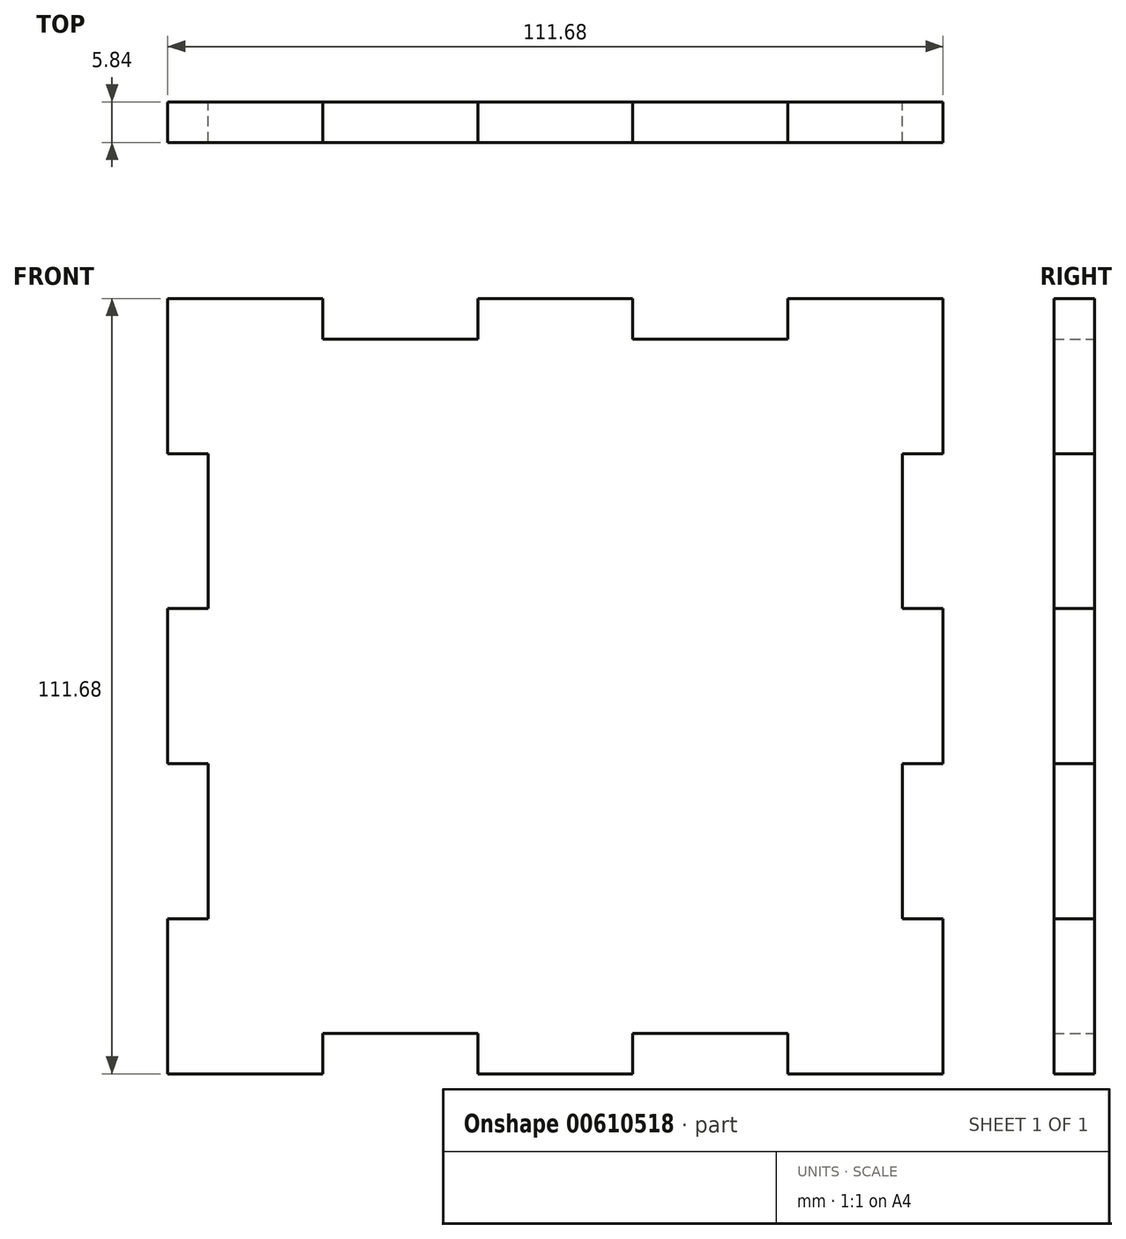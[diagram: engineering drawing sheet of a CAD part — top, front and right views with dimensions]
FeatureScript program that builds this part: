
annotation { "Feature Type Name" : "Feature", "Feature Type Description" : "" }
export const myFeature = defineFeature(function(context is Context, id is Id, definition is map)
    precondition{}
    {
        {
            var Q0;
            Q0=qCreatedBy(makeId("Front.planeOp"),FACE);
            var sketch = newSketch(context, id + "F0", { "sketchPlane" : qUnion([Q0])});
            skLineSegment(sketch, "E0.bottom", {"start": v(-50, 50) * mm, "end": v(50, 50) * mm});
            skLineSegment(sketch, "E0.top", {"start": v(-50, -50) * mm, "end": v(50, -50) * mm});
            skLineSegment(sketch, "E0.left", {"start": v(-50, 50) * mm, "end": v(-50, -50) * mm});
            skLineSegment(sketch, "E0.right", {"start": v(50, 50) * mm, "end": v(50, -50) * mm});
            skLineSegment(sketch, "E1.bottom", {"start": v(-55.84, 55.84) * mm, "end": v(-33.5, 55.84) * mm});
            skLineSegment(sketch, "E1.top", {"start": v(-55.84, -55.84) * mm, "end": v(-33.5, -55.84) * mm});
            skLineSegment(sketch, "E1.left", {"start": v(-55.84, 55.84) * mm, "end": v(-55.84, 33.5) * mm});
            skLineSegment(sketch, "E1.right", {"start": v(55.84, 55.84) * mm, "end": v(55.84, 33.5) * mm});
            skPoint(sketch, "E1.middle", {"position": v(0, 0) * mm});
            skLineSegment(sketch, "E2", {"start": v(-33.5, 50) * mm, "end": v(-33.5, 55.84) * mm});
            skLineSegment(sketch, "E3", {"start": v(-11.17, 50) * mm, "end": v(-11.17, 55.84) * mm});
            skPoint(sketch, "E3.endSnap0", {"position": v(0, 55.84) * mm});
            skLineSegment(sketch, "E4", {"start": v(11.17, 50) * mm, "end": v(11.17, 55.84) * mm});
            skLineSegment(sketch, "E5", {"start": v(33.5, 50) * mm, "end": v(33.5, 55.84) * mm});
            skLineSegment(sketch, "E6.trimOffspring", {"start": v(-11.17, 55.84) * mm, "end": v(11.17, 55.84) * mm});
            skLineSegment(sketch, "E7.trimOffspring", {"start": v(33.5, 55.84) * mm, "end": v(55.84, 55.84) * mm});
            skLineSegment(sketch, "E8", {"start": v(-50, 33.5) * mm, "end": v(-55.84, 33.5) * mm});
            skLineSegment(sketch, "E9", {"start": v(-50, 11.17) * mm, "end": v(-55.84, 11.17) * mm});
            skLineSegment(sketch, "E10", {"start": v(-50, -11.17) * mm, "end": v(-55.84, -11.17) * mm});
            skLineSegment(sketch, "E11", {"start": v(-50, -33.5) * mm, "end": v(-55.84, -33.5) * mm});
            skLineSegment(sketch, "E12.trimOffspring", {"start": v(-55.84, 11.17) * mm, "end": v(-55.84, -11.17) * mm});
            skLineSegment(sketch, "E13.trimOffspring", {"start": v(-55.84, -33.5) * mm, "end": v(-55.84, -55.84) * mm});
            skLineSegment(sketch, "E14", {"start": v(-33.5, -50) * mm, "end": v(-33.5, -55.84) * mm});
            skLineSegment(sketch, "E15", {"start": v(-11.17, -50) * mm, "end": v(-11.17, -55.84) * mm});
            skLineSegment(sketch, "E16", {"start": v(11.17, -50) * mm, "end": v(11.17, -55.84) * mm});
            skLineSegment(sketch, "E17", {"start": v(33.5, -50) * mm, "end": v(33.5, -55.84) * mm});
            skLineSegment(sketch, "E18.trimOffspring", {"start": v(-11.17, -55.84) * mm, "end": v(11.17, -55.84) * mm});
            skLineSegment(sketch, "E19.trimOffspring", {"start": v(33.5, -55.84) * mm, "end": v(55.84, -55.84) * mm});
            skLineSegment(sketch, "E20", {"start": v(50, -33.5) * mm, "end": v(55.84, -33.5) * mm});
            skLineSegment(sketch, "E21", {"start": v(50, -11.17) * mm, "end": v(55.84, -11.17) * mm});
            skLineSegment(sketch, "E22", {"start": v(50, 11.17) * mm, "end": v(55.84, 11.17) * mm});
            skLineSegment(sketch, "E23", {"start": v(50, 33.5) * mm, "end": v(55.84, 33.5) * mm});
            skLineSegment(sketch, "E24.trimOffspring", {"start": v(55.84, 11.17) * mm, "end": v(55.84, -11.17) * mm});
            skLineSegment(sketch, "E25.trimOffspring", {"start": v(55.84, -33.5) * mm, "end": v(55.84, -55.84) * mm});
            skSolve(sketch);
        }
        {
            var Q0;
            Q0 = qSketchRegion(id + "F0", true);
            extrude(context, id + "F1", {"entities" : qUnion([Q0]), "depth" : 5.84 * mm, "offsetDistance" : 25 * mm});
        }
    });
